# Revit family: Поли-Групп_КлапанОбратныйEAZ-SMR_DN100-1600
name_source: partatom
category: Арматура трубопроводов
units: mm (PartAtom-declared; Revit-internal decimal feet)

## family parameters
Всегда вертикально = Да
На основе рабочей плоскости = Нет
Общий = Нет
При загрузке вырезать с полостями = Нет
Размер круглого соединителя = Использовать диаметр
Тип детали = Клапан - Вставляется

## types (30) — shared parameters
ADSK_URL страницы изделия = https://www.polycorr.ru
ADSK_Версия Revit = 2019
ADSK_Единица измерения = шт.
ADSK_Завод-изготовитель = ООО ПК «Поли-Групп»
ADSK_Код изделия = 107-8874
ADSK_Количество = 1
ADSK_Материал = Высокопрочный чугун GGG-40
ADSK_Материал наименование = Высокопрочный чугун с шаровидным графитом (GGG-40)
r = 10 мм
Изображение типоразмера = <Нет>
Класс герметичности = А по ГОСТ Р 9544-2015
Материал Диска = Высокопрочный чугун с шаровидным графитом (GGG-40)
Назначение = Для предотвращения обратного потока среды на трубопроводах
Покрытие = Высококачественное эпоксидное покрытие толщиной 300 мкм.
Рабочая среда = Питьевая вода, техническая вода, канализационные стоки, морская вода.
Разработчик = https://3dbim.pro
Срок службы = 50 лет
ТВ = КлапанОбратныйEAZ-SMR_DN100-1600_Поли-Групп
Температура рабочей среды = 0 до +70°С
Тип присоединения = Фланцевое
zero-valued in all types: Крутящий момент

## per-type parameters (varying)
| type | ADSK_Марка | ADSK_Масса | ADSK_Масса_Текст | ADSK_Наименование | ADSK_Наименование краткое | D | D2 | D3 | D4 | DN | L | PN | b | f | Вал_r | Диск_t | Уши_h | Уши_h2 |
| 200-16 | EAZ-DCh-3 DN200 PN16 | 56 | 56 | Клапан обратный EAZ SMR дисковый с наклонным седлом фланцевый DN200 PN16 | Клапан обратный EAZ SMR DN200 PN16 | 340 мм | 266 мм | 210 мм | 240 мм | 200 мм | 230 мм | 16.0 бары | 20 мм | 3 мм | 34 мм | 20 мм | 340 мм | 266 мм |
| 250-16 | EAZ-DCh-3 DN250 PN16 | 81 | 81 | Клапан обратный EAZ SMR дисковый с наклонным седлом фланцевый DN250 PN16 | Клапан обратный EAZ SMR DN250 PN16 | 400 мм | 266 мм | 260 мм | 290 мм | 250 мм | 250 мм | 16.0 бары | 22 мм | 3 мм | 40 мм | 25 мм | 400 мм | 266 мм |
| 300-16 | EAZ-DCh-3 DN300 PN16 | 106 | 106 | Клапан обратный EAZ SMR дисковый с наклонным седлом фланцевый DN300 PN16 | Клапан обратный EAZ SMR DN300 PN16 | 460 мм | 370 мм | 310 мм | 340 мм | 300 мм | 270 мм | 16.0 бары | 25 мм | 4 мм | 46 мм | 30 мм | 460 мм | 370 мм |
| 350-16 | EAZ-DCh-3 DN350 PN16 | 150 | 150 | Клапан обратный EAZ SMR дисковый с наклонным седлом фланцевый DN350 PN16 | Клапан обратный EAZ SMR DN350 PN16 | 520 мм | 370 мм | 360 мм | 390 мм | 350 мм | 290 мм | 16.0 бары | 27 мм | 4 мм | 52 мм | 35 мм | 520 мм | 370 мм |
| 400-16 | EAZ-DCh-3 DN400 PN16 | 205 | 205 | Клапан обратный EAZ SMR дисковый с наклонным седлом фланцевый DN400 PN16 | Клапан обратный EAZ SMR DN400 PN16 | 580 мм | 480 мм | 410 мм | 440 мм | 400 мм | 310 мм | 16.0 бары | 28 мм | 4 мм | 58 мм | 40 мм | 580 мм | 480 мм |
| 450-16 | EAZ-DCh-3 DN450 PN16 | 232 | 232 | Клапан обратный EAZ SMR дисковый с наклонным седлом фланцевый DN450 PN16 | Клапан обратный EAZ SMR DN450 PN16 | 640 мм | 480 мм | 460 мм | 490 мм | 450 мм | 330 мм | 16.0 бары | 32 мм | 4 мм | 64 мм | 45 мм | 640 мм | 480 мм |
| 500-16 | EAZ-DCh-3 DN500 PN16 | 395 | 395 | Клапан обратный EAZ SMR дисковый с наклонным седлом фланцевый DN500 PN16 | Клапан обратный EAZ SMR DN500 PN16 | 715 мм | 609 мм | 510 мм | 540 мм | 500 мм | 350 мм | 16.0 бары | 32 мм | 4 мм | 72 мм | 50 мм | 715 мм | 609 мм |
| 600-16 | EAZ-DCh-3 DN600 PN16 | 425 | 425 | Клапан обратный EAZ SMR дисковый с наклонным седлом фланцевый DN600 PN16 | Клапан обратный EAZ SMR DN600 PN16 | 840 мм | 682 мм | 610 мм | 640 мм | 600 мм | 390 мм | 16.0 бары | 36 мм | 5 мм | 84 мм | 60 мм | 840 мм | 682 мм |
| 700-16 | EAZ-DCh-3 DN700 PN16 | 536 | 536 | Клапан обратный EAZ SMR дисковый с наклонным седлом фланцевый DN700 PN16 | Клапан обратный EAZ SMR DN700 PN16 | 910 мм | 794 мм | 710 мм | 740 мм | 700 мм | 430 мм | 16.0 бары | 40 мм | 5 мм | 91 мм | 70 мм | 910 мм | 794 мм |
| 800-16 | EAZ-DCh-3 DN800 PN16 | 750 | 750 | Клапан обратный EAZ SMR дисковый с наклонным седлом фланцевый DN800 PN16 | Клапан обратный EAZ SMR DN800 PN16 | 1025 мм | 901 мм | 810 мм | 840 мм | 800 мм | 470 мм | 16.0 бары | 43 мм | 5 мм | 103 мм | 80 мм | 1025 мм | 901 мм |
| 900-16 | EAZ-DCh-3 DN900 PN16 | 865 | 865 | Клапан обратный EAZ SMR дисковый с наклонным седлом фланцевый DN900 PN16 | Клапан обратный EAZ SMR DN900 PN16 | 1125 мм | 1001 мм | 910 мм | 940 мм | 900 мм | 510 мм | 16.0 бары | 47 мм | 5 мм | 113 мм | 90 мм | 1125 мм | 1001 мм |
| 1000-16 | EAZ-DCh-3 DN1000 PN16 | 1280 | 1280 | Клапан обратный EAZ SMR дисковый с наклонным седлом фланцевый DN1000 PN16 | Клапан обратный EAZ SMR DN1000 PN16 | 1255 мм | 1112 мм | 1010 мм | 1040 мм | 1000 мм | 550 мм | 16.0 бары | 50 мм | 5 мм | 126 мм | 100 мм | 1255 мм | 1112 мм |
| 1200-16 | EAZ-DCh-3 DN1200 PN16 | 2025 | 2025 | Клапан обратный EAZ SMR дисковый с наклонным седлом фланцевый DN1200 PN16 | Клапан обратный EAZ SMR DN1200 PN16 | 1485 мм | 1328 мм | 1210 мм | 1240 мм | 1200 мм | 630 мм | 16.0 бары | 57 мм | 5 мм | 149 мм | 120 мм | 1485 мм | 1328 мм |
| 1400-16 | EAZ-DCh-3 DN1400 PN16 | 3050 | 3050 | Клапан обратный EAZ SMR дисковый с наклонным седлом фланцевый DN1400 PN16 | Клапан обратный EAZ SMR DN1400 PN16 | 1685 мм | 1530 мм | 1410 мм | 1440 мм | 1400 мм | 710 мм | 16.0 бары | 60 мм | 5 мм | 169 мм | 140 мм | 1685 мм | 1530 мм |
| 1600-16 | EAZ-DCh-3 DN1600 PN16 | 3850 | 3850 | Клапан обратный EAZ SMR дисковый с наклонным седлом фланцевый DN1600 PN16 | Клапан обратный EAZ SMR DN1600 PN16 | 1930 мм | 1750 мм | 1610 мм | 1640 мм | 1600 мм | 790 мм | 16.0 бары | 65 мм | 5 мм | 193 мм | 160 мм | 1930 мм | 1750 мм |
| 200-10 | EAZ-DCh-3 DN200 PN10 | 52 | 52 | Клапан обратный EAZ SMR дисковый с наклонным седлом фланцевый DN200 PN10 | Клапан обратный EAZ SMR DN200 PN10 | 340 мм | 266 мм | 210 мм | 240 мм | 200 мм | 230 мм | 10.0 бары | 20 мм | 3 мм | 34 мм | 20 мм | 340 мм | 266 мм |
| 250-10 | EAZ-DCh-3 DN250 PN10 | 60 | 60 | Клапан обратный EAZ SMR дисковый с наклонным седлом фланцевый DN250 PN10 | Клапан обратный EAZ SMR DN250 PN10 | 400 мм | 266 мм | 260 мм | 290 мм | 250 мм | 250 мм | 10.0 бары | 22 мм | 3 мм | 40 мм | 25 мм | 400 мм | 266 мм |
| 300-10 | EAZ-DCh-3 DN300 PN10 | 95 | 95 | Клапан обратный EAZ SMR дисковый с наклонным седлом фланцевый DN300 PN10 | Клапан обратный EAZ SMR DN300 PN10 | 445 мм | 370 мм | 310 мм | 340 мм | 300 мм | 270 мм | 10.0 бары | 25 мм | 4 мм | 45 мм | 30 мм | 445 мм | 370 мм |
| 350-10 | EAZ-DCh-3 DN350 PN10 | 132 | 132 | Клапан обратный EAZ SMR дисковый с наклонным седлом фланцевый DN350 PN10 | Клапан обратный EAZ SMR DN350 PN10 | 520 мм | 370 мм | 360 мм | 390 мм | 350 мм | 290 мм | 10.0 бары | 27 мм | 4 мм | 52 мм | 35 мм | 520 мм | 370 мм |
| 400-10 | EAZ-DCh-3 DN400 PN10 | 191 | 191 | Клапан обратный EAZ SMR дисковый с наклонным седлом фланцевый DN400 PN10 | Клапан обратный EAZ SMR DN400 PN10 | 565 мм | 480 мм | 410 мм | 440 мм | 400 мм | 310 мм | 10.0 бары | 25 мм | 4 мм | 57 мм | 40 мм | 565 мм | 480 мм |
| 450-10 | EAZ-DCh-3 DN450 PN10 | 220 | 220 | Клапан обратный EAZ SMR дисковый с наклонным седлом фланцевый DN450 PN10 | Клапан обратный EAZ SMR DN450 PN10 | 615 мм | 480 мм | 460 мм | 490 мм | 450 мм | 330 мм | 10.0 бары | 27 мм | 4 мм | 62 мм | 45 мм | 615 мм | 480 мм |
| 500-10 | EAZ-DCh-3 DN500 PN10 | 317 | 317 | Клапан обратный EAZ SMR дисковый с наклонным седлом фланцевый DN500 PN10 | Клапан обратный EAZ SMR DN500 PN10 | 670 мм | 582 мм | 510 мм | 540 мм | 500 мм | 350 мм | 10.0 бары | 27 мм | 4 мм | 67 мм | 50 мм | 670 мм | 582 мм |
| 600-10 | EAZ-DCh-3 DN600 PN10 | 398 | 398 | Клапан обратный EAZ SMR дисковый с наклонным седлом фланцевый DN600 PN10 | Клапан обратный EAZ SMR DN600 PN10 | 780 мм | 682 мм | 610 мм | 640 мм | 600 мм | 390 мм | 10.0 бары | 30 мм | 5 мм | 78 мм | 60 мм | 780 мм | 682 мм |
| 700-10 | EAZ-DCh-3 DN700 PN10 | 475 | 475 | Клапан обратный EAZ SMR дисковый с наклонным седлом фланцевый DN700 PN10 | Клапан обратный EAZ SMR DN700 PN10 | 895 мм | 794 мм | 710 мм | 740 мм | 700 мм | 430 мм | 10.0 бары | 33 мм | 5 мм | 90 мм | 70 мм | 895 мм | 794 мм |
| 800-10 | EAZ-DCh-3 DN800 PN10 | 728 | 728 | Клапан обратный EAZ SMR дисковый с наклонным седлом фланцевый DN800 PN10 | Клапан обратный EAZ SMR DN800 PN10 | 1015 мм | 901 мм | 810 мм | 840 мм | 800 мм | 470 мм | 10.0 бары | 35 мм | 5 мм | 102 мм | 80 мм | 1015 мм | 901 мм |
| 900-10 | EAZ-DCh-3 DN900 PN10 | 840 | 840 | Клапан обратный EAZ SMR дисковый с наклонным седлом фланцевый DN900 PN10 | Клапан обратный EAZ SMR DN900 PN10 | 1115 мм | 1001 мм | 910 мм | 940 мм | 900 мм | 510 мм | 10.0 бары | 38 мм | 5 мм | 112 мм | 90 мм | 1115 мм | 1001 мм |
| 1000-10 | EAZ-DCh-3 DN1000 PN10 | 1080 | 1080 | Клапан обратный EAZ SMR дисковый с наклонным седлом фланцевый DN1000 PN10 | Клапан обратный EAZ SMR DN1000 PN10 | 1230 мм | 1112 мм | 1010 мм | 1040 мм | 1000 мм | 550 мм | 10.0 бары | 40 мм | 5 мм | 123 мм | 100 мм | 1230 мм | 1112 мм |
| 1200-10 | EAZ-DCh-3 DN1200 PN10 | 1810 | 1810 | Клапан обратный EAZ SMR дисковый с наклонным седлом фланцевый DN1200 PN10 | Клапан обратный EAZ SMR DN1200 PN10 | 1455 мм | 1328 мм | 1210 мм | 1240 мм | 1200 мм | 630 мм | 10.0 бары | 45 мм | 5 мм | 146 мм | 120 мм | 1455 мм | 1328 мм |
| 1400-10 | EAZ-DCh-3 DN1400 PN10 | 2890 | 2890 | Клапан обратный EAZ SMR дисковый с наклонным седлом фланцевый DN1400 PN10 | Клапан обратный EAZ SMR DN1400 PN10 | 1675 мм | 1530 мм | 1410 мм | 1440 мм | 1400 мм | 710 мм | 10.0 бары | 46 мм | 5 мм | 168 мм | 140 мм | 1675 мм | 1530 мм |
| 1600-10 | EAZ-DCh-3 DN1600 PN10 | 3500 | 3500 | Клапан обратный EAZ SMR дисковый с наклонным седлом фланцевый DN1600 PN10 | Клапан обратный EAZ SMR DN1600 PN10 | 1915 мм | 1750 мм | 1610 мм | 1640 мм | 1600 мм | 790 мм | 10.0 бары | 49 мм | 5 мм | 192 мм | 160 мм | 1915 мм | 1750 мм |
